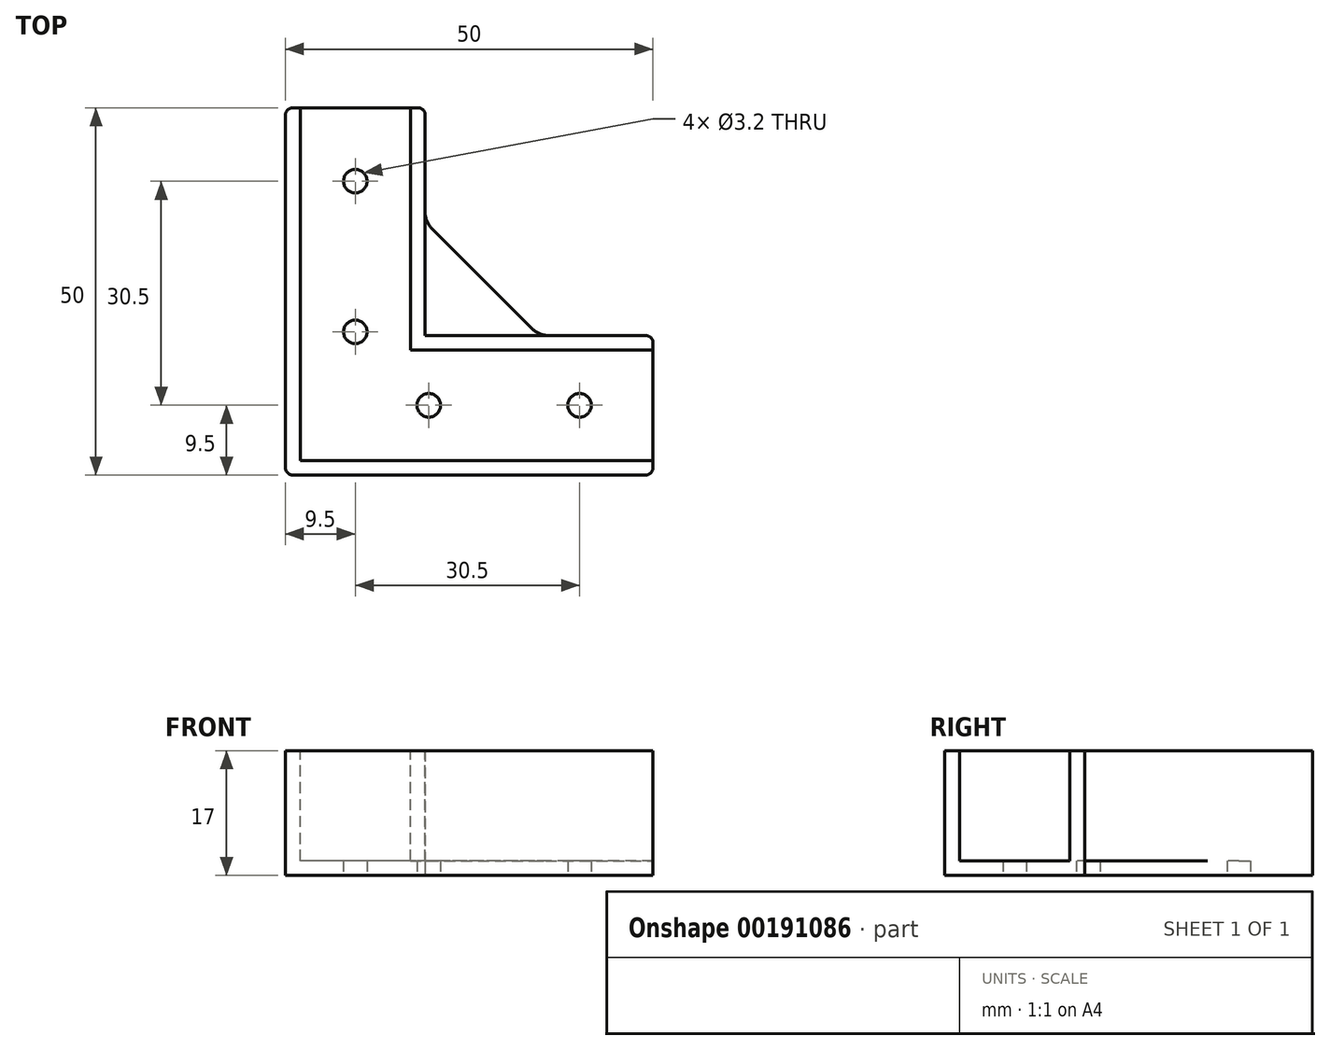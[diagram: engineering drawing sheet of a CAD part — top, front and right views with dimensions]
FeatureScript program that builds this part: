
annotation { "Feature Type Name" : "Feature", "Feature Type Description" : "" }
export const myFeature = defineFeature(function(context is Context, id is Id, definition is map)
    precondition{}
    {
        {
            var Q0;
            Q0=qCreatedBy(makeId("Top.planeOp"),FACE);
            var sketch = newSketch(context, id + "F0", { "sketchPlane" : qUnion([Q0])});
            skLineSegment(sketch, "E0.bottom", {"start": v(25, -25) * mm, "end": v(-25, -25) * mm, "construction": true});
            skLineSegment(sketch, "E0.top", {"start": v(25, 25) * mm, "end": v(-25, 25) * mm, "construction": true});
            skLineSegment(sketch, "E0.left", {"start": v(25, -25) * mm, "end": v(25, 25) * mm, "construction": true});
            skLineSegment(sketch, "E0.right", {"start": v(-25, -25) * mm, "end": v(-25, 25) * mm, "construction": true});
            skPoint(sketch, "E0.middle", {"position": v(0, 0) * mm});
            skLineSegment(sketch, "E1", {"start": v(-6, 25) * mm, "end": v(-6, -25) * mm, "construction": true});
            skLineSegment(sketch, "E2", {"start": v(-25, -6) * mm, "end": v(25, -6) * mm, "construction": true});
            skLineSegment(sketch, "E3", {"start": v(-25, 25) * mm, "end": v(-25, -25) * mm});
            skLineSegment(sketch, "E4", {"start": v(25, -25) * mm, "end": v(25, -6) * mm});
            skLineSegment(sketch, "E5", {"start": v(-25, -25) * mm, "end": v(25, -25) * mm});
            skLineSegment(sketch, "E6", {"start": v(25, -6) * mm, "end": v(-6, -6) * mm});
            skLineSegment(sketch, "E7", {"start": v(-6, -6) * mm, "end": v(-6, 25) * mm});
            skLineSegment(sketch, "E8", {"start": v(-6, 25) * mm, "end": v(-25, 25) * mm});
            skLineSegment(sketch, "E9", {"start": v(9.5, -6) * mm, "end": v(-6, 9.5) * mm});
            skSolve(sketch);
        }
        {
            var Q0;
            Q0 = qSketchRegion(id + "F0", true);
            extrude(context, id + "F1", {"entities" : qUnion([Q0]), "depth" : 17 * mm, "offsetDistance" : 25 * mm});
        }
        {
            var Q0;
            Q0=makeQuery(id+"F1.opExtrude","CAP_FACE",FACE,{"disambiguationData":[OSD([sQuery(id+"F0.wireOp",EDGE,"E3"),sQuery(id+"F0.wireOp",EDGE,"E4"),sQuery(id+"F0.wireOp",EDGE,"E5"),sQuery(id+"F0.wireOp",EDGE,"E6"),sQuery(id+"F0.wireOp",EDGE,"E7"),sQuery(id+"F0.wireOp",EDGE,"E8")])],"isStart":false});
            var sketch = newSketch(context, id + "F2", { "sketchPlane" : qUnion([Q0])});
            skLineSegment(sketch, "E10.0", {"start": v(-23, 25) * mm, "end": v(-23, -23) * mm});
            skLineSegment(sketch, "E11.0", {"start": v(-8, 25) * mm, "end": v(-8, -6) * mm});
            skLineSegment(sketch, "E12.0", {"start": v(-6, -8) * mm, "end": v(25, -8) * mm});
            skLineSegment(sketch, "E13.0", {"start": v(25, -23) * mm, "end": v(-23, -23) * mm});
            skLineSegment(sketch, "E14", {"start": v(-8, -6) * mm, "end": v(-8, -8) * mm});
            skLineSegment(sketch, "E15", {"start": v(-6, -8) * mm, "end": v(-8, -8) * mm});
            skLineSegment(sketch, "E16", {"start": v(-23, 25) * mm, "end": v(-8, 25) * mm});
            skLineSegment(sketch, "E17", {"start": v(25, -23) * mm, "end": v(25, -8) * mm});
            skSolve(sketch);
        }
        {
            var Q0;
            Q0 = qSketchRegion(id + "F2", true);
            extrude(context, id + "F3", {"entities" : qUnion([Q0]), "operationType" : NewBodyOperationType.REMOVE, "oppositeDirection" : true, "depth" : 15 * mm, "offsetDistance" : 25 * mm});
        }
        {
            var Q0;
            Q0=makeQuery(id+"F1.opExtrude","CAP_FACE",FACE,{"disambiguationData":[OSD([sQuery(id+"F0.wireOp",EDGE,"E3"),sQuery(id+"F0.wireOp",EDGE,"E4"),sQuery(id+"F0.wireOp",EDGE,"E5"),sQuery(id+"F0.wireOp",EDGE,"E6"),sQuery(id+"F0.wireOp",EDGE,"E7"),sQuery(id+"F0.wireOp",EDGE,"E8")])],"isStart":true});
            var sketch = newSketch(context, id + "F4", { "sketchPlane" : qUnion([Q0])});
            skLineSegment(sketch, "E18", {"start": v(25, 15.5) * mm, "end": v(-25, 15.5) * mm, "construction": true});
            skLineSegment(sketch, "E19", {"start": v(-15.5, -25) * mm, "end": v(-15.5, 25) * mm, "construction": true});
            skCircle(sketch, "E20", {"center": v(15, 15.5) * mm, "radius": 1.6 * mm});
            skCircle(sketch, "E21", {"center": v(-5.5, 15.5) * mm, "radius": 1.6 * mm});
            skLineSegment(sketch, "E22", {"start": v(25, 6) * mm, "end": v(25, -25) * mm, "construction": true});
            skLineSegment(sketch, "E23", {"start": v(-25, 25) * mm, "end": v(25, -25) * mm, "construction": true});
            skCircle(sketch, "E24.MirrorC", {"center": v(-15.5, 5.5) * mm, "radius": 1.6 * mm});
            skCircle(sketch, "E25.MirrorC", {"center": v(-15.5, -15) * mm, "radius": 1.6 * mm});
            skSolve(sketch);
        }
        {
            var Q0;
            Q0 = qSketchRegion(id + "F4", true);
            extrude(context, id + "F5", {"entities" : qUnion([Q0]), "operationType" : NewBodyOperationType.REMOVE, "endBound" : BoundingType.UP_TO_NEXT, "oppositeDirection" : true, "depth" : 25 * mm, "offsetDistance" : 25 * mm});
        }
        {
            var Q0;
            Q0=makeQuery(id+"F1.opExtrude","SWEPT_EDGE",EDGE,{"disambiguationData":[OSD([sQuery(id+"F0.wireOp",EDGE,"E4"),sQuery(id+"F0.wireOp",EDGE,"E5")])]});
            var Q1;
            Q1=makeQuery(id+"F3.boolean.opBoolean","COPY",EDGE,{"derivedFrom":makeQuery(id+"F3.opExtrude","SWEPT_EDGE",EDGE,{"disambiguationData":[OSD([sQuery(id+"F0.wireOp",EDGE,"E4"),sQuery(id+"F2.wireOp",EDGE,"E13.0"),sQuery(id+"F2.wireOp",EDGE,"E17")])]})});
            var Q2;
            Q2=makeQuery(id+"F3.boolean.opBoolean","COPY",EDGE,{"derivedFrom":makeQuery(id+"F3.opExtrude","SWEPT_EDGE",EDGE,{"disambiguationData":[OSD([sQuery(id+"F0.wireOp",EDGE,"E4"),sQuery(id+"F2.wireOp",EDGE,"E12.0"),sQuery(id+"F2.wireOp",EDGE,"E17")])]})});
            var Q3;
            Q3=makeQuery(id+"F1.opExtrude","SWEPT_EDGE",EDGE,{"disambiguationData":[OSD([sQuery(id+"F0.wireOp",EDGE,"E4"),sQuery(id+"F0.wireOp",EDGE,"E6")])]});
            var Q4;
            Q4=makeQuery(id+"F1.opExtrude","SWEPT_EDGE",EDGE,{"disambiguationData":[OSD([sQuery(id+"F0.wireOp",EDGE,"E3"),sQuery(id+"F0.wireOp",EDGE,"E5")])]});
            var Q5;
            Q5=makeQuery(id+"F1.opExtrude","SWEPT_EDGE",EDGE,{"disambiguationData":[OSD([sQuery(id+"F0.wireOp",EDGE,"E3"),sQuery(id+"F0.wireOp",EDGE,"E8")])]});
            var Q6;
            Q6=makeQuery(id+"F3.boolean.opBoolean","COPY",EDGE,{"derivedFrom":makeQuery(id+"F3.opExtrude","SWEPT_EDGE",EDGE,{"disambiguationData":[OSD([sQuery(id+"F0.wireOp",EDGE,"E8"),sQuery(id+"F2.wireOp",EDGE,"E11.0"),sQuery(id+"F2.wireOp",EDGE,"E16")])]})});
            var Q7;
            Q7=makeQuery(id+"F3.boolean.opBoolean","COPY",EDGE,{"derivedFrom":makeQuery(id+"F3.opExtrude","SWEPT_EDGE",EDGE,{"disambiguationData":[OSD([sQuery(id+"F0.wireOp",EDGE,"E8"),sQuery(id+"F2.wireOp",EDGE,"E10.0"),sQuery(id+"F2.wireOp",EDGE,"E16")])]})});
            var Q8;
            Q8=makeQuery(id+"F1.opExtrude","SWEPT_EDGE",EDGE,{"disambiguationData":[OSD([sQuery(id+"F0.wireOp",EDGE,"E7"),sQuery(id+"F0.wireOp",EDGE,"E8")])]});
            fillet(context, id + "F6", {"entities" : qUnion([Q0, Q1, Q2, Q3, Q4, Q5, Q6, Q7, Q8]), "radius" : 1 * mm, "tangentPropagation" : true, "allowEdgeOverflow" : false});
        }
        {
            var Q0;
            {var subQ0=sQuery(id+"F0.wireOp",EDGE,"E8");var subQ1=sQuery(id+"F0.wireOp",EDGE,"E7");var subQ2=sQuery(id+"F0.wireOp",EDGE,"E6");var subQ3=sQuery(id+"F0.wireOp",EDGE,"E4");var subQ4=sQuery(id+"F0.wireOp",EDGE,"E9");Q0=makeQuery(id+"F3.boolean.opBoolean","SPLIT",FACE,{"disambiguationData":[TD([makeQuery(id+"F1.opExtrude","SWEPT_FACE",FACE,{"disambiguationData":[OSD([subQ2])]})])],"derivedFrom":makeQuery(id+"F1.opExtrude","CAP_FACE",FACE,{"disambiguationData":[OSD([sQuery(id+"F0.wireOp",EDGE,"E3"),subQ3,sQuery(id+"F0.wireOp",EDGE,"E5"),subQ2,subQ1,subQ0,subQ4])],"isStart":false})});}
            var sketch = newSketch(context, id + "F7", { "sketchPlane" : qUnion([Q0])});
            skLineSegment(sketch, "E26", {"start": v(9.5, -6) * mm, "end": v(-6, -6) * mm});
            skLineSegment(sketch, "E27", {"start": v(-6, -6) * mm, "end": v(-6, 9.5) * mm});
            skLineSegment(sketch, "E28", {"start": v(-6, 9.5) * mm, "end": v(9.5, -6) * mm});
            skSolve(sketch);
        }
        {
            var Q0;
            Q0 = qSketchRegion(id + "F7", true);
            extrude(context, id + "F8", {"entities" : qUnion([Q0]), "operationType" : NewBodyOperationType.REMOVE, "oppositeDirection" : true, "depth" : 15 * mm, "offsetDistance" : 25 * mm});
        }
        {
            var Q0;
            Q0=makeQuery(id+"F1.opExtrude","SWEPT_EDGE",EDGE,{"disambiguationData":[OSD([sQuery(id+"F0.wireOp",EDGE,"E7"),sQuery(id+"F0.wireOp",EDGE,"E9")])]});
            var Q1;
            Q1=makeQuery(id+"F1.opExtrude","SWEPT_EDGE",EDGE,{"disambiguationData":[OSD([sQuery(id+"F0.wireOp",EDGE,"E6"),sQuery(id+"F0.wireOp",EDGE,"E9")])]});
            fillet(context, id + "F9", {"entities" : qUnion([Q0, Q1]), "radius" : 3 * mm, "tangentPropagation" : true, "allowEdgeOverflow" : false});
        }
    });
